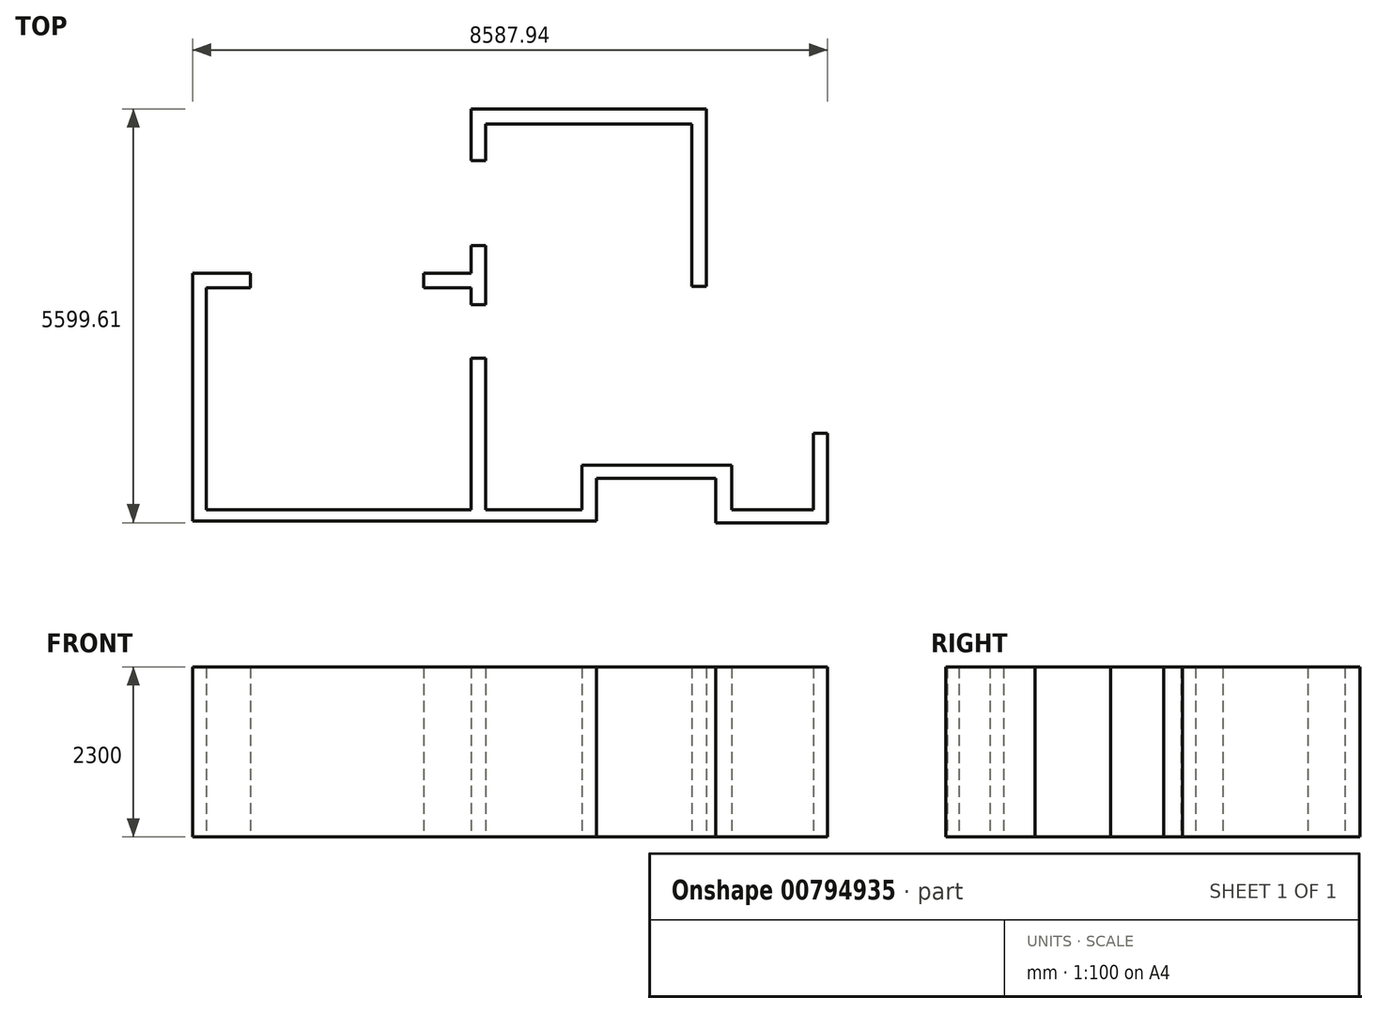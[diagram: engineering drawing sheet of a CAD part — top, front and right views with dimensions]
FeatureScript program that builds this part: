
annotation { "Feature Type Name" : "Feature", "Feature Type Description" : "" }
export const myFeature = defineFeature(function(context is Context, id is Id, definition is map)
    precondition{}
    {
        {
            var Q0;
            Q0=qCreatedBy(makeId("Top.planeOp"),FACE);
            var sketch = newSketch(context, id + "F0", { "sketchPlane" : qUnion([Q0])});
            skLineSegment(sketch, "E0", {"start": v(3747.94, 2413.89) * mm, "end": v(3747.94, 4613.89) * mm});
            skLineSegment(sketch, "E1", {"start": v(3747.94, 4613.89) * mm, "end": v(957.94, 4613.89) * mm});
            skLineSegment(sketch, "E2", {"start": v(957.94, 4613.89) * mm, "end": v(957.94, 4113.89) * mm});
            skLineSegment(sketch, "E3", {"start": v(957.94, 4113.89) * mm, "end": v(757.94, 4113.89) * mm});
            skLineSegment(sketch, "E4", {"start": v(757.94, 4113.89) * mm, "end": v(757.94, 2963.89) * mm});
            skLineSegment(sketch, "E5", {"start": v(757.94, 2963.89) * mm, "end": v(957.94, 2963.89) * mm});
            skLineSegment(sketch, "E6", {"start": v(957.94, 2963.89) * mm, "end": v(957.94, 2163.89) * mm});
            skLineSegment(sketch, "E7", {"start": v(957.94, 2163.89) * mm, "end": v(757.94, 2163.89) * mm});
            skLineSegment(sketch, "E8", {"start": v(757.94, 2163.89) * mm, "end": v(757.94, 2393.89) * mm});
            skLineSegment(sketch, "E9", {"start": v(757.94, 2393.89) * mm, "end": v(117.94, 2393.89) * mm});
            skLineSegment(sketch, "E10", {"start": v(117.94, 2393.89) * mm, "end": v(117.94, 2593.89) * mm});
            skLineSegment(sketch, "E11", {"start": v(117.94, 2593.89) * mm, "end": v(-2222.06, 2593.89) * mm});
            skLineSegment(sketch, "E12", {"start": v(-2222.06, 2593.89) * mm, "end": v(-2222.06, 2393.89) * mm});
            skLineSegment(sketch, "E13", {"start": v(-2222.06, 2393.89) * mm, "end": v(-2822.06, 2393.89) * mm});
            skLineSegment(sketch, "E14", {"start": v(-2822.06, 2393.89) * mm, "end": v(-2822.06, -606.11) * mm});
            skLineSegment(sketch, "E15", {"start": v(-2822.06, -606.11) * mm, "end": v(757.94, -606.11) * mm});
            skLineSegment(sketch, "E16", {"start": v(957.94, -606.11) * mm, "end": v(2257.94, -606.11) * mm});
            skLineSegment(sketch, "E17", {"start": v(2257.94, -606.11) * mm, "end": v(2257.94, -6.11) * mm});
            skLineSegment(sketch, "E18", {"start": v(2257.94, -6.11) * mm, "end": v(4287.94, -6.11) * mm});
            skLineSegment(sketch, "E19", {"start": v(4287.94, -6.11) * mm, "end": v(4287.94, -606.11) * mm});
            skLineSegment(sketch, "E20", {"start": v(4287.94, -606.11) * mm, "end": v(5387.94, -606.11) * mm});
            skLineSegment(sketch, "E21", {"start": v(5387.94, -606.11) * mm, "end": v(5387.94, 423.89) * mm});
            skLineSegment(sketch, "E22", {"start": v(757.94, 1443.89) * mm, "end": v(957.94, 1443.89) * mm});
            skLineSegment(sketch, "E23", {"start": v(957.94, 1443.89) * mm, "end": v(957.94, -606.11) * mm});
            skLineSegment(sketch, "E24", {"start": v(-2222.06, 2593.89) * mm, "end": v(-3007.35, 2593.89) * mm});
            skLineSegment(sketch, "E25", {"start": v(-3007.35, 2593.89) * mm, "end": v(-3007.35, -763.34) * mm});
            skLineSegment(sketch, "E26", {"start": v(-3007.35, -763.34) * mm, "end": v(2457.95, -763.34) * mm});
            skLineSegment(sketch, "E27", {"start": v(2457.95, -763.34) * mm, "end": v(2457.95, -185.99) * mm});
            skLineSegment(sketch, "E28", {"start": v(4070.7, -185.99) * mm, "end": v(4070.7, -785.3) * mm});
            skLineSegment(sketch, "E29", {"start": v(4070.7, -785.3) * mm, "end": v(5580.6, -785.3) * mm});
            skLineSegment(sketch, "E30", {"start": v(5580.6, -785.3) * mm, "end": v(5580.6, 423.89) * mm});
            skLineSegment(sketch, "E31", {"start": v(5580.6, 423.89) * mm, "end": v(5387.94, 423.89) * mm});
            skLineSegment(sketch, "E32", {"start": v(757.94, 2963.89) * mm, "end": v(757.94, 2593.89) * mm});
            skLineSegment(sketch, "E33", {"start": v(757.94, 2593.89) * mm, "end": v(117.94, 2593.89) * mm});
            skLineSegment(sketch, "E34", {"start": v(757.94, 4113.89) * mm, "end": v(757.94, 4814.3) * mm});
            skLineSegment(sketch, "E35", {"start": v(757.94, 4814.3) * mm, "end": v(3940.7, 4814.3) * mm});
            skLineSegment(sketch, "E36", {"start": v(3940.7, 4814.3) * mm, "end": v(3940.7, 2413.89) * mm});
            skLineSegment(sketch, "E37", {"start": v(3940.7, 2413.89) * mm, "end": v(3747.94, 2413.89) * mm});
            skLineSegment(sketch, "E38", {"start": v(757.94, 1443.89) * mm, "end": v(757.94, -606.11) * mm});
            skLineSegment(sketch, "E39", {"start": v(4070.7, -185.99) * mm, "end": v(2457.95, -185.99) * mm});
            skSolve(sketch);
        }
        {
            var Q0;
            Q0 = qSketchRegion(id + "F0", true);
            extrude(context, id + "F1", {"entities" : qUnion([Q0]), "depth" : 2300 * mm, "offsetDistance" : 25 * mm});
        }
    });
